# Revit family: 702-40-103-DN50-600
name_source: partatom
category: Pipe Accessories
units: mm (PartAtom-declared; Revit-internal decimal feet)

## family parameters
Always vertical = Yes
Cut with Voids When Loaded = No
Part Type = Valve - Breaks Into
Round Connector Dimension = Use Diameter
Shared = No
Work Plane-Based = No

## types (14) — shared parameters
DN050 = Yes
DN050_PN10/16 = 702-050-40-134
DN065 = Yes
DN065_PN10/16 = 702-065-40-134
DN080 = Yes
DN080_PN10/16 = 702-080-40-134
DN100 = Yes
DN100_PN10/16 = 702-100-40-134
DN125 = Yes
DN125_PN10/16 = 702-125-40-134
DN150 = Yes
DN150_PN10/16 = 702-150-40-134
DN200 = Yes
DN200_PN10 = 702-200-40-034
DN250_PN10 = 702-250-40-034
DN300 = Yes
DN300_PN10 = 702-300-40-034
DN350 = Yes
DN350_PN10 = 702-350-40-034
DN400 = Yes
DN400_PN10 = 702-400-40-034
DN450 = Yes
DN450_PN10 = 702-450-40-034
DN500 = Yes
DN500_PN10 = 702-500-40-034
DN600 = Yes
DN600_PN10 = 702-600-40-034
Description_ = AVK KNIFE GATE VALVE
Search_table = 702-40-103-DN50-600
URL product pages = https://www.avkvalves.com

## per-type parameters (varying)
| type | B2_Ref | Body_width | Bonnet_height | Bonnet_height_2 | Cut_Height | D | Fillet_Radius | Flange_Thickness | H | H1 | H2 | H3 | HW_Rib | H_Ref | ID | L | L2 | Name_Ref | Neck_Rod | Nominal Diameter (DN) | W | W2 | W3 | W4 |
| DN 050 | 78 mm  [stored 0.255906 ft] | 87 mm | 268 mm | 119 mm | 15 mm  [stored 0.0492126 ft] | 80 mm  [stored 0.262467 ft] | 5 mm  [stored 0.0164042 ft] | 5 mm  [stored 0.0164042 ft] | 415 mm | 147 mm | 14 mm  [stored 0.0459318 ft] | 494 mm | 145 mm | 113 mm | 25 mm  [stored 0.082021 ft] | 43 mm  [stored 0.141076 ft] | 47 mm | 141 mm | 10 mm  [stored 0.0328084 ft] | 50 mm  [stored 0.164042 ft] | 130 mm | 54 mm  [stored 0.177165 ft] | 65 mm  [stored 0.213255 ft] | 54 mm  [stored 0.177165 ft] |
| DN 065 | 86 mm | 95 mm  [stored 0.31168 ft] | 296 mm | 130 mm | 15 mm  [stored 0.0492126 ft] | 80 mm  [stored 0.262467 ft] | 5 mm  [stored 0.0164042 ft] | 5 mm  [stored 0.0164042 ft] | 456 mm | 160 mm | 14 mm  [stored 0.0459318 ft] | 541 mm | 145 mm | 124 mm | 33 mm | 46 mm  [stored 0.150919 ft] | 51 mm | 155 mm | 10 mm  [stored 0.0328084 ft] | 65 mm  [stored 0.213255 ft] | 143 mm | 60 mm  [stored 0.19685 ft] | 72 mm | 60 mm  [stored 0.19685 ft] |
| DN 080 | 110 mm | 122 mm | 309 mm | 139 mm | 15 mm  [stored 0.0492126 ft] | 100 mm  [stored 0.328084 ft] | 5 mm  [stored 0.0164042 ft] | 5 mm  [stored 0.0164042 ft] | 486 mm | 177 mm | 14 mm  [stored 0.0459318 ft] | 592 mm | 195 mm | 159 mm | 40 mm  [stored 0.131234 ft] | 46 mm  [stored 0.150919 ft] | 51 mm | 198 mm | 10 mm  [stored 0.0328084 ft] | 80 mm  [stored 0.262467 ft] | 183 mm | 76 mm  [stored 0.249344 ft] | 92 mm | 76 mm  [stored 0.249344 ft] |
| DN 100 | 121 mm | 135 mm | 352 mm | 157 mm | 30 mm  [stored 0.0984252 ft] | 100 mm  [stored 0.328084 ft] | 10 mm  [stored 0.0328084 ft] | 5 mm  [stored 0.0164042 ft] | 549 mm | 197 mm | 14 mm  [stored 0.0459318 ft] | 664 mm | 195 mm | 175 mm | 50 mm  [stored 0.164042 ft] | 52 mm | 57 mm | 219 mm | 10 mm  [stored 0.0328084 ft] | 100 mm  [stored 0.328084 ft] | 202 mm | 84 mm  [stored 0.275591 ft] | 101 mm | 84 mm  [stored 0.275591 ft] |
| DN 125 | 137 mm | 153 mm | 378 mm | 174 mm | 30 mm  [stored 0.0984252 ft] | 125 mm | 10 mm  [stored 0.0328084 ft] | 5 mm  [stored 0.0164042 ft] | 610 mm | 232 mm | 16 mm  [stored 0.0524934 ft] | 740 mm | 195 mm | 198 mm | 63 mm | 56 mm  [stored 0.183727 ft] | 62 mm | 248 mm | 10 mm  [stored 0.0328084 ft] | 125 mm | 229 mm | 95 mm  [stored 0.31168 ft] | 115 mm | 95 mm  [stored 0.31168 ft] |
| DN 150 | 160 mm | 178 mm | 424 mm | 197 mm | 30 mm  [stored 0.0984252 ft] | 160 mm | 10 mm  [stored 0.0328084 ft] | 5 mm  [stored 0.0164042 ft] | 691 mm | 267 mm | 16 mm  [stored 0.0524934 ft] | 840 mm | 270 mm | 231 mm | 75 mm  [stored 0.246063 ft] | 56 mm  [stored 0.183727 ft] | 62 mm | 289 mm | 10 mm  [stored 0.0328084 ft] | 150 mm | 267 mm | 111 mm | 134 mm | 111 mm |
| DN 200 | 196 mm | 217 mm | 544 mm | 249 mm | 45 mm  [stored 0.147638 ft] | 190 mm | 15 mm  [stored 0.0492126 ft] | 10 mm  [stored 0.0328084 ft] | 871 mm | 327 mm | 19 mm  [stored 0.062336 ft] | 1053 mm | 240 mm | 283 mm | 100 mm  [stored 0.328084 ft] | 60 mm  [stored 0.19685 ft] | 66 mm  [stored 0.216535 ft] | 353 mm | 20 mm  [stored 0.0656168 ft] | 200 mm | 326 mm | 136 mm | 163 mm | 136 mm |
| DN 300 | 271 mm | 301 mm | 789 mm | 348 mm | 45 mm  [stored 0.147638 ft] | 190 mm | 15 mm  [stored 0.0492126 ft] | 15 mm  [stored 0.0492126 ft] | 1217 mm | 428 mm | 19 mm  [stored 0.062336 ft] | 1462 mm | 310 mm | 391 mm | 150 mm | 78 mm  [stored 0.255906 ft] | 86 mm | 489 mm | 30 mm  [stored 0.0984252 ft] | 300 mm | 451 mm | 188 mm | 226 mm | 188 mm |
| DN 350 | 311 mm | 345 mm | 882 mm | 395 mm | 60 mm  [stored 0.19685 ft] | 250 mm | 20 mm  [stored 0.0656168 ft] | 15 mm  [stored 0.0492126 ft] | 1381 mm | 499 mm | 25 mm  [stored 0.082021 ft] | 1666 mm | 310 mm | 449 mm | 175 mm | 78 mm  [stored 0.255906 ft] | 86 mm | 561 mm | 30 mm  [stored 0.0984252 ft] | 350 mm | 518 mm | 216 mm | 259 mm | 216 mm |
| DN 400 | 346 mm | 384 mm | 992 mm | 440 mm | 60 mm  [stored 0.19685 ft] | 250 mm | 20 mm  [stored 0.0656168 ft] | 20 mm  [stored 0.0656168 ft] | 1541 mm | 549 mm | 25 mm  [stored 0.082021 ft] | 1854 mm | 280 mm | 499 mm | 200 mm | 90 mm  [stored 0.295276 ft] | 99 mm  [stored 0.324803 ft] | 624 mm | 40 mm  [stored 0.131234 ft] | 400 mm | 576 mm | 240 mm | 288 mm | 240 mm |
| DN 450 | 371 mm | 412 mm | 1121 mm | 490 mm | 60 mm  [stored 0.19685 ft] | 300 mm | 20 mm  [stored 0.0656168 ft] | 20 mm  [stored 0.0656168 ft] | 1715 mm | 594 mm | 25 mm  [stored 0.082021 ft] | 2049 mm | 380 mm | 536 mm | 225 mm | 90 mm  [stored 0.295276 ft] | 99 mm  [stored 0.324803 ft] | 670 mm | 40 mm  [stored 0.131234 ft] | 450 mm | 618 mm | 258 mm | 309 mm | 258 mm |
| DN 500 | 419 mm | 465 mm | 1219 mm | 536 mm | 75 mm  [stored 0.246063 ft] | 300 mm | 25 mm  [stored 0.082021 ft] | 20 mm  [stored 0.0656168 ft] | 1875 mm | 656 mm | 25 mm  [stored 0.082021 ft] | 2249 mm | 380 mm | 605 mm | 250 mm | 95 mm  [stored 0.31168 ft] | 105 mm | 756 mm | 40 mm  [stored 0.131234 ft] | 500 mm | 698 mm | 291 mm | 349 mm | 291 mm |
| DN 600 | 490 mm | 545 mm | 1413 mm | 620 mm | 75 mm  [stored 0.246063 ft] | 300 mm | 25 mm  [stored 0.082021 ft] | 20 mm  [stored 0.0656168 ft] | 2169 mm | 756 mm | 25 mm  [stored 0.082021 ft] | 2602 mm | 380 mm | 708 mm | 300 mm | 105 mm | 116 mm | 885 mm | 40 mm  [stored 0.131234 ft] | 600 mm | 817 mm | 340 mm | 409 mm | 340 mm |
| DN 250 | 237 mm | 263 mm | 671 mm | 299 mm | 45 mm  [stored 0.147638 ft] | 190 mm | 15 mm  [stored 0.0492126 ft] | 10 mm  [stored 0.0328084 ft] | 1046 mm | 375 mm | 19 mm  [stored 0.062336 ft] | 1263 mm | 240 mm | 342 mm | 125 mm | 68 mm  [stored 0.223097 ft] | 75 mm  [stored 0.246063 ft] | 428 mm | 20 mm  [stored 0.0656168 ft] | 250 mm | 395 mm | 165 mm | 198 mm | 165 mm |

note: [stored X ft] marks values corroborated as IEEE doubles in the binary element streams (Revit-internal decimal feet)

## geometry (parser evidence)
native form markers: Sweep x6
no freeform markers — native parametric forms only
